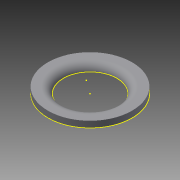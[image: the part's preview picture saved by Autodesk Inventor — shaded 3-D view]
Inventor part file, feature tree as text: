
AUTODESK INVENTOR PART (.ipt)
format: ipt  version: 2015 SP1 (Build 190203100, 203)  size: 116,224 bytes
history: native  units: mm
features: reference x8, sketch x3, extrude x2, other x1, fillet x1, projected_geometry x1
ambient origin geometry x8: Origin, YZ Plane, XZ Plane, XY Plane, X Axis, Y Axis, Z Axis, Center Point
bodies: Body1 (feature_tree)
feature tree (16):
  other  "Sólido1"
  extrude  "Extrusión1"  Depth=55.0mm
  extrude  "Extrusión2"  Depth=2.0mm TaperAngle=0.0deg
  fillet  "Empalme1"  Radius=5.0mm
  sketch  "Boceto3"
  sketch  "Boceto1"  dims[d0=35.0mm d1=55.0mm]
  reference  "Referencia1"
  reference  "Referencia2"
  reference  "Referencia3"
  reference  "Referencia4"
  sketch  "Boceto2"  dims[d2=4.0mm d3=0.0mm d4=2.0mm d5=0.0mm d6=5.0mm]
  reference  "Referencia5"
  reference  "Referencia6"
  reference  "Referencia7"
  reference  "Referencia8"
  projected_geometry  "Contorno proyectado1"
